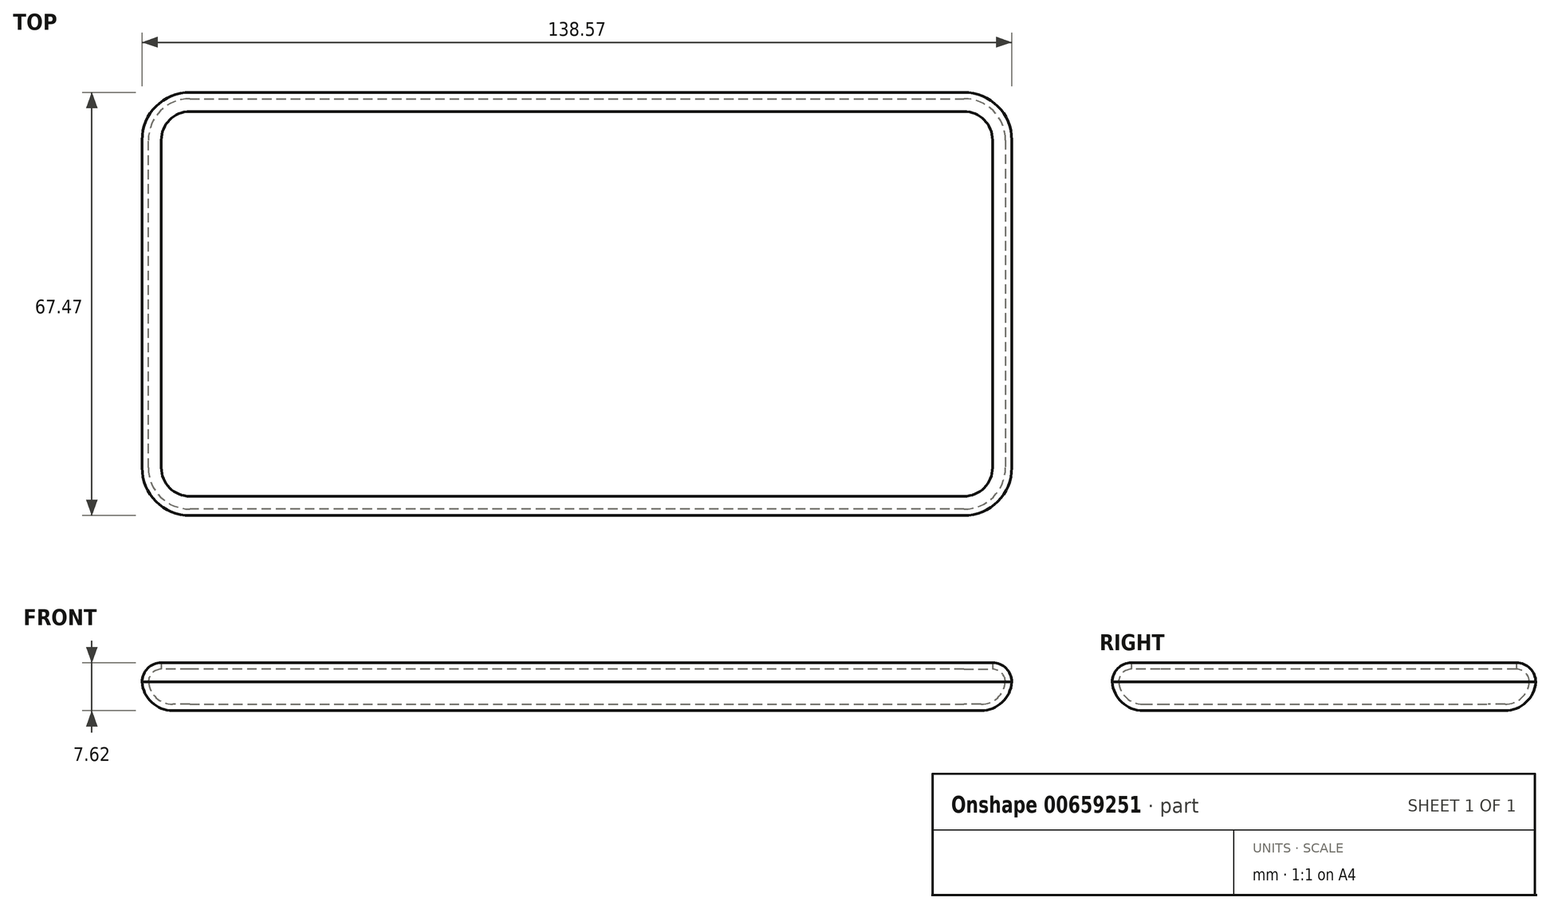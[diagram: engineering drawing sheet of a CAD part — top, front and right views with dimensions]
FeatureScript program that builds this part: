
annotation { "Feature Type Name" : "Feature", "Feature Type Description" : "" }
export const myFeature = defineFeature(function(context is Context, id is Id, definition is map)
    precondition{}
    {
        {
            var Q0;
            Q0=qCreatedBy(makeId("Top.planeOp"),FACE);
            var sketch = newSketch(context, id + "F0", { "sketchPlane" : qUnion([Q0])});
            skLineSegment(sketch, "E0.bottom", {"start": v(-70, 33.42) * mm, "end": v(68.57, 33.42) * mm});
            skLineSegment(sketch, "E0.top", {"start": v(-70, -34.05) * mm, "end": v(68.57, -34.05) * mm});
            skLineSegment(sketch, "E0.left", {"start": v(-70, 33.42) * mm, "end": v(-70, -34.05) * mm});
            skLineSegment(sketch, "E0.right", {"start": v(68.57, 33.42) * mm, "end": v(68.57, -34.05) * mm});
            skSolve(sketch);
        }
        {
            var Q0;
            Q0=makeQuery(id+"F0.imprint","IMPRINT",FACE,{"disambiguationData":[TD([[makeQuery(id+"F0.imprint","IMPRINT",EDGE,{"derivedFrom":sQuery(id+"F0.wireOp",EDGE,"E0.bottom")}),-1.0]])]});
            extrude(context, id + "F1", {"entities" : qUnion([Q0]), "depth" : 7.62 * mm, "offsetDistance" : 25.4 * mm});
        }
        {
            var Q0;
            Q0=makeQuery(id+"F1.opExtrude","SWEPT_EDGE",EDGE,{"disambiguationData":[OSD([sQuery(id+"F0.wireOp",EDGE,"E0.top"),sQuery(id+"F0.wireOp",EDGE,"E0.left")])]});
            var Q1;
            Q1=makeQuery(id+"F1.opExtrude","SWEPT_EDGE",EDGE,{"disambiguationData":[OSD([sQuery(id+"F0.wireOp",EDGE,"E0.top"),sQuery(id+"F0.wireOp",EDGE,"E0.right")])]});
            var Q2;
            Q2=makeQuery(id+"F1.opExtrude","SWEPT_EDGE",EDGE,{"disambiguationData":[OSD([sQuery(id+"F0.wireOp",EDGE,"E0.bottom"),sQuery(id+"F0.wireOp",EDGE,"E0.right")])]});
            var Q3;
            Q3=makeQuery(id+"F1.opExtrude","SWEPT_EDGE",EDGE,{"disambiguationData":[OSD([sQuery(id+"F0.wireOp",EDGE,"E0.bottom"),sQuery(id+"F0.wireOp",EDGE,"E0.left")])]});
            fillet(context, id + "F2", {"entities" : qUnion([Q0, Q1, Q2, Q3]), "radius" : 7.62 * mm, "tangentPropagation" : true, "allowEdgeOverflow" : false});
        }
        {
            var Q0;
            Q0=makeQuery(id+"F1.opExtrude","CAP_EDGE",EDGE,{"disambiguationData":[OSD([sQuery(id+"F0.wireOp",EDGE,"E0.bottom")])],"isStart":false});
            fillet(context, id + "F3", {"entities" : qUnion([Q0]), "radius" : 3.07 * mm, "tangentPropagation" : true, "allowEdgeOverflow" : false});
        }
        {
            var Q0;
            Q0=makeQuery(id+"F1.opExtrude","CAP_EDGE",EDGE,{"disambiguationData":[OSD([sQuery(id+"F0.wireOp",EDGE,"E0.left")])],"isStart":true});
            fillet(context, id + "F4", {"entities" : qUnion([Q0]), "radius" : 4.9 * mm, "tangentPropagation" : true, "allowEdgeOverflow" : false});
        }
        {
            var Q0;
            Q0=makeQuery(id+"F1.opExtrude","CAP_FACE",FACE,{"disambiguationData":[OSD([sQuery(id+"F0.wireOp",EDGE,"E0.bottom"),sQuery(id+"F0.wireOp",EDGE,"E0.top"),sQuery(id+"F0.wireOp",EDGE,"E0.left"),sQuery(id+"F0.wireOp",EDGE,"E0.right")])],"isStart":false});
            shell(context, id + "F5", {"entities" : qUnion([Q0]), "thickness" : 1.02 * mm});
        }
    });
